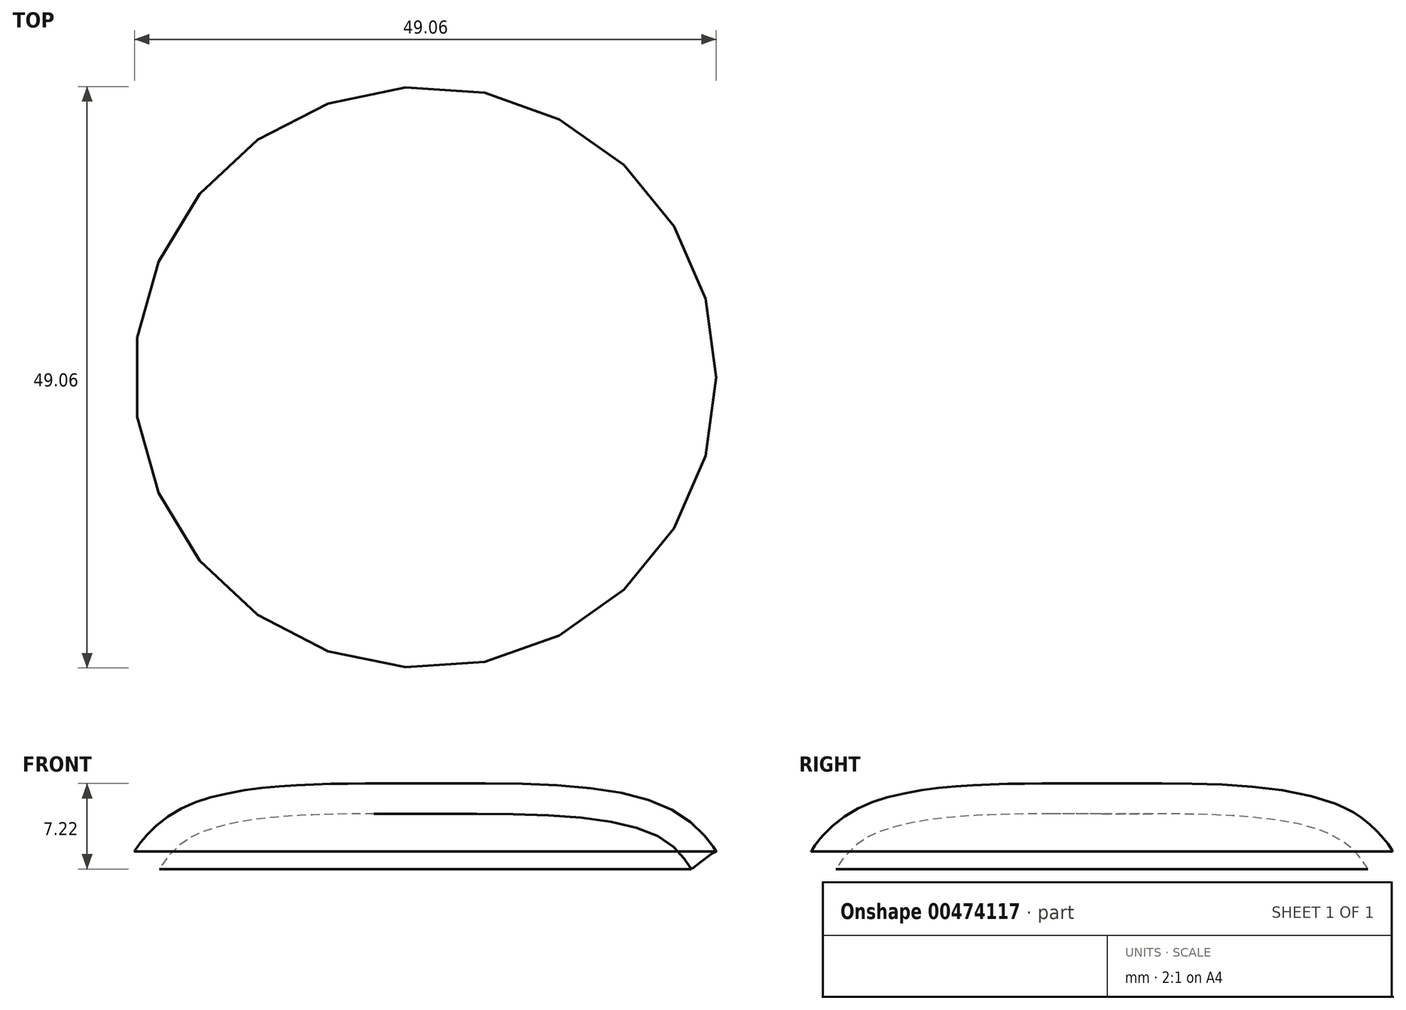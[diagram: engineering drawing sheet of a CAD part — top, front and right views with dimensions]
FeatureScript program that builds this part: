
annotation { "Feature Type Name" : "Feature", "Feature Type Description" : "" }
export const myFeature = defineFeature(function(context is Context, id is Id, definition is map)
    precondition{}
    {
        {
            var Q0;
            Q0=qCreatedBy(makeId("Front.planeOp"),FACE);
            var sketch = newSketch(context, id + "F0", { "sketchPlane" : qUnion([Q0])});
            skLineSegment(sketch, "E0", {"start": v(0, 0) * mm, "end": v(0, -2.54) * mm});
            skFitSpline(sketch, "E1", {"points": [v(0, -2.54) * mm, v(20.13, -4.71) * mm, v(22.41, -7.16) * mm, v(22.47, -7.16) * mm, v(24.48, -5.7) * mm, v(24.53, -5.7) * mm, v(21.44, -2.54) * mm, v(0, 0) * mm], "startDerivative": vector(83.28, 0.75) * mm, "endDerivative": vector(-83.33, -1.12) * mm});
            skSolve(sketch);
        }
        {
            var Q0;
            Q0=makeQuery(id+"F0.imprint","IMPRINT",FACE,{"disambiguationData":[TD([[makeQuery(id+"F0.imprint","IMPRINT",EDGE,{"derivedFrom":sQuery(id+"F0.wireOp",EDGE,"E0")}),1.0]])]});
            var Q1;
            Q1=sQuery(id+"F0.wireOp",EDGE,"E0");
            revolve(context, id + "F1", {"entities" : qUnion([Q0]), "axis" : qUnion([Q1]), "revolveType" : RevolveType.FULL});
        }
    });
